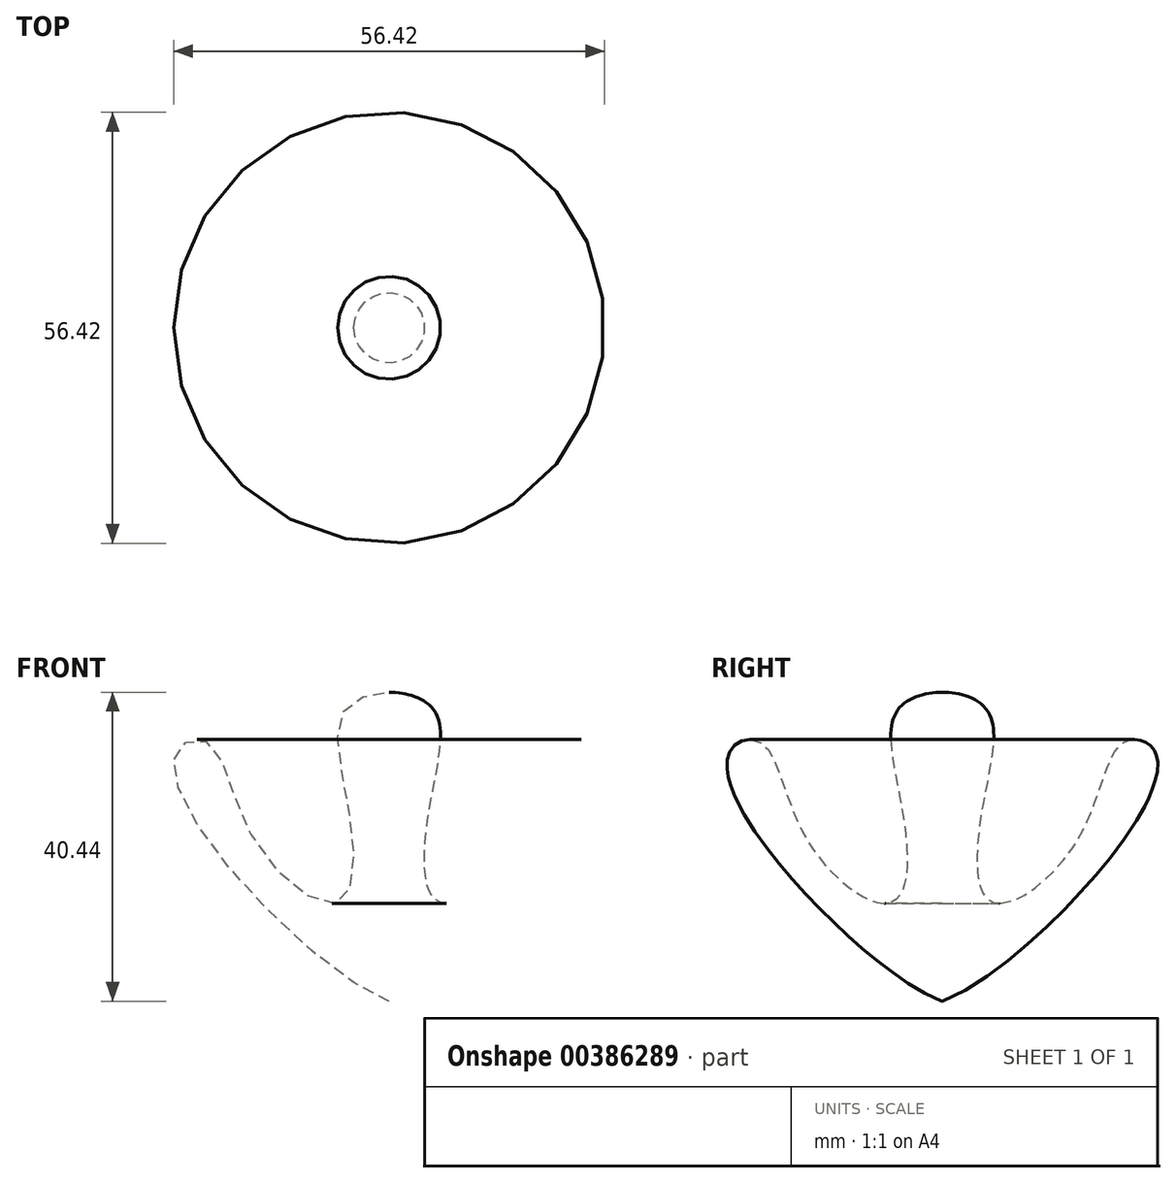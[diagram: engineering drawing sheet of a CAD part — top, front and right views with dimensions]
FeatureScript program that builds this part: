
annotation { "Feature Type Name" : "Feature", "Feature Type Description" : "" }
export const myFeature = defineFeature(function(context is Context, id is Id, definition is map)
    precondition{}
    {
        {
            var Q0;
            Q0=qCreatedBy(makeId("Front.planeOp"),FACE);
            var sketch = newSketch(context, id + "F0", { "sketchPlane" : qUnion([Q0])});
            skLineSegment(sketch, "E0", {"start": v(0, 51.85) * mm, "end": v(0, -38.96) * mm});
            skFitSpline(sketch, "E1", {"points": [v(0, 0) * mm, v(-23.49, 20.74) * mm, v(-27.7, 32.92) * mm, v(-23.73, 33.86) * mm, v(-17.63, 20.98) * mm, v(-6.57, 12.96) * mm, v(-5.1, 24.1) * mm, v(-6.15, 37.6) * mm, v(0, 40.44) * mm], "startDerivative": vector(-92.16, 31.28) * mm, "endDerivative": vector(80.86, 0) * mm});
            skLineSegment(sketch, "E2", {"start": v(0, 40.44) * mm, "end": v(-26.06, 40.44) * mm});
            skLineSegment(sketch, "E3", {"start": v(-26.06, 40.44) * mm, "end": v(-27.95, 40.44) * mm});
            skSolve(sketch);
        }
        {
            var Q0;
            {var subQ0=sQuery(id+"F0.wireOp",EDGE,"E1");var subQ1=sQuery(id+"F0.wireOp",EDGE,"E0");var subQ2=makeQuery(id+"F0.imprint","INTERSECT",VERTEX,{"derivedFrom":[subQ1,subQ0]});Q0=makeQuery(id+"F0.imprint","IMPRINT",FACE,{"disambiguationData":[TD([[makeQuery(id+"F0.imprint","IMPRINT",EDGE,{"disambiguationData":[TD([[subQ2,-1.0]])],"derivedFrom":subQ0}),-1.0]])]});}
            var Q1;
            Q1=sQuery(id+"F0.wireOp",EDGE,"E0");
            revolve(context, id + "F1", {"entities" : qUnion([Q0]), "axis" : qUnion([Q1]), "revolveType" : RevolveType.FULL});
        }
    });
